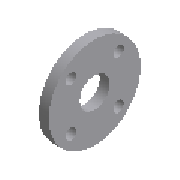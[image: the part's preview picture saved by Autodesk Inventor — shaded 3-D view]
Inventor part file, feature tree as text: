
AUTODESK INVENTOR PART (.ipt)
format: ipt  version: 2025 (Build 290162010, 162A)  size: 188,416 bytes
history: native  units: mm (DEFAULTED — no unit token found)
features: other x5, revolve x1, extrude x1, pattern_circular x1
ambient origin geometry x8: Origin, YZ Plane, XZ Plane, XY Plane, X Axis, Y Axis, Z Axis, Center Point
bodies: Solid1 (feature_tree)
feature tree (8):
  revolve  "Revolution1"  Angle=90.0deg
  extrude  "Extrusion1"  Depth=670.0mm
  pattern_circular  "Circular Pattern1"  [2 undecoded]
  other  "Work Axis1"
  other  "Work Point1"
  other  "Work Axis2"
  other  "Work Point2"
  other  "Work Point3"
note: 2 required parameter values undecoded (feature->parameter linkage not recoverable at this tier; creation-order binding heuristic only, values carry confidence <= 0.55)
